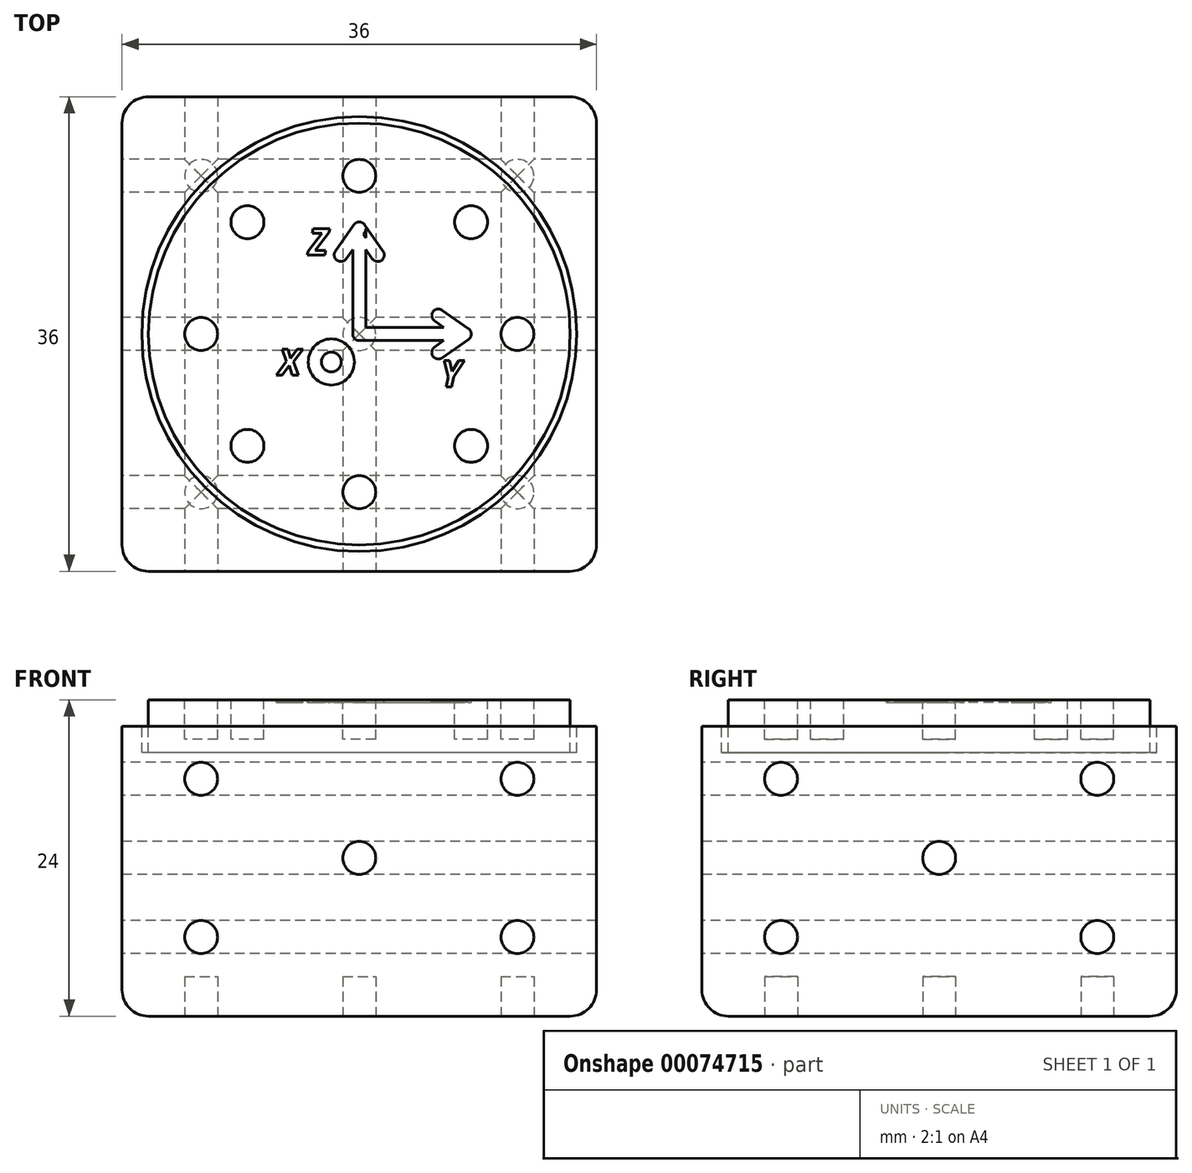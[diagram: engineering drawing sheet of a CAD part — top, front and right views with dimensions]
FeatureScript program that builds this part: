
annotation { "Feature Type Name" : "Feature", "Feature Type Description" : "" }
export const myFeature = defineFeature(function(context is Context, id is Id, definition is map)
    precondition{}
    {
        {
            var Q0;
            Q0=qCreatedBy(makeId("Right.planeOp"),FACE);
            var sketch = newSketch(context, id + "F0", { "sketchPlane" : qUnion([Q0])});
            skLineSegment(sketch, "E0.rect.bottom", {"start": v(18, -12) * mm, "end": v(-18, -12) * mm});
            skLineSegment(sketch, "E0.rect.top", {"start": v(18, 12) * mm, "end": v(-18, 12) * mm});
            skLineSegment(sketch, "E0.rect.left", {"start": v(18, -12) * mm, "end": v(18, 12) * mm});
            skLineSegment(sketch, "E0.rect.right", {"start": v(-18, -12) * mm, "end": v(-18, 12) * mm});
            skPoint(sketch, "E0.rect.middle", {"position": v(0, 0) * mm});
            skSolve(sketch);
        }
        {
            var Q0;
            Q0=makeQuery(id+"F0.imprint","IMPRINT",FACE,{"disambiguationData":[TD([[makeQuery(id+"F0.imprint","IMPRINT",EDGE,{"derivedFrom":sQuery(id+"F0.wireOp",EDGE,"E0.rect.bottom")}),-1.0]])]});
            extrude(context, id + "F1", {"entities" : qUnion([Q0]), "endBound" : BoundingType.SYMMETRIC, "depth" : 36 * mm});
        }
        {
            var Q0;
            Q0=makeQuery(id+"F1.opExtrude","SWEPT_FACE",FACE,{"disambiguationData":[OSD([sQuery(id+"F0.wireOp",EDGE,"E0.rect.right")])]});
            var sketch = newSketch(context, id + "F2", { "sketchPlane" : qUnion([Q0])});
            skLineSegment(sketch, "E1.0", {"start": v(-12, 6) * mm, "end": v(-12, -6) * mm, "construction": true});
            skLineSegment(sketch, "E1.1", {"start": v(12, 6) * mm, "end": v(-12, 6) * mm, "construction": true});
            skLineSegment(sketch, "E1.2", {"start": v(12, -6) * mm, "end": v(12, 6) * mm, "construction": true});
            skLineSegment(sketch, "E1.3", {"start": v(-12, -6) * mm, "end": v(12, -6) * mm, "construction": true});
            skLineSegment(sketch, "E2", {"start": v(-12, 6) * mm, "end": v(12, -6) * mm, "construction": true});
            skCircle(sketch, "E3", {"center": v(-12, 6) * mm, "radius": 1.25 * mm});
            skCircle(sketch, "E4", {"center": v(12, 6) * mm, "radius": 1.25 * mm});
            skCircle(sketch, "E5", {"center": v(0, 0) * mm, "radius": 1.25 * mm});
            skCircle(sketch, "E6", {"center": v(-12, -6) * mm, "radius": 1.25 * mm});
            skCircle(sketch, "E7", {"center": v(12, -6) * mm, "radius": 1.25 * mm});
            skSolve(sketch);
        }
        {
            var Q0;
            Q0=makeQuery(id+"F1.opExtrude","CAP_FACE",FACE,{"disambiguationData":[OSD([sQuery(id+"F0.wireOp",EDGE,"E0.rect.bottom"),sQuery(id+"F0.wireOp",EDGE,"E0.rect.top"),sQuery(id+"F0.wireOp",EDGE,"E0.rect.left"),sQuery(id+"F0.wireOp",EDGE,"E0.rect.right")])],"isStart":true});
            var sketch = newSketch(context, id + "F3", { "sketchPlane" : qUnion([Q0])});
            skLineSegment(sketch, "E8.0", {"start": v(-12, -6) * mm, "end": v(12, -6) * mm, "construction": true});
            skLineSegment(sketch, "E8.1", {"start": v(-12, 6) * mm, "end": v(-12, -6) * mm, "construction": true});
            skLineSegment(sketch, "E8.2", {"start": v(12, 6) * mm, "end": v(-12, 6) * mm, "construction": true});
            skLineSegment(sketch, "E8.3", {"start": v(12, -6) * mm, "end": v(12, 6) * mm, "construction": true});
            skLineSegment(sketch, "E9", {"start": v(-12, 6) * mm, "end": v(12, -6) * mm, "construction": true});
            skCircle(sketch, "E10", {"center": v(-12, 6) * mm, "radius": 1.25 * mm});
            skCircle(sketch, "E11", {"center": v(-12, -6) * mm, "radius": 1.25 * mm});
            skCircle(sketch, "E12", {"center": v(0, 0) * mm, "radius": 1.25 * mm});
            skCircle(sketch, "E13", {"center": v(12, -6) * mm, "radius": 1.25 * mm});
            skCircle(sketch, "E14", {"center": v(12, 6) * mm, "radius": 1.25 * mm});
            skSolve(sketch);
        }
        {
            var Q0;
            Q0=makeQuery(id+"F1.opExtrude","SWEPT_FACE",FACE,{"disambiguationData":[OSD([sQuery(id+"F0.wireOp",EDGE,"E0.rect.top")])]});
            var sketch = newSketch(context, id + "F4", { "sketchPlane" : qUnion([Q0])});
            skCircle(sketch, "E15", {"center": v(0, 0) * mm, "radius": 16 * mm, "construction": true});
            skCircle(sketch, "E16", {"center": v(0, 0) * mm, "radius": 12 * mm, "construction": true});
            skCircle(sketch, "E17", {"center": v(12, 0) * mm, "radius": 1.25 * mm});
            skCircle(sketch, "E18.1.0", {"center": v(8.49, 8.49) * mm, "radius": 1.25 * mm});
            skCircle(sketch, "E18.2.0", {"center": v(0, 12) * mm, "radius": 1.25 * mm});
            skCircle(sketch, "E18.3.0", {"center": v(-8.49, 8.49) * mm, "radius": 1.25 * mm});
            skCircle(sketch, "E18.4.0", {"center": v(-12, 0) * mm, "radius": 1.25 * mm});
            skCircle(sketch, "E18.5.0", {"center": v(-8.49, -8.49) * mm, "radius": 1.25 * mm});
            skCircle(sketch, "E18.6.0", {"center": v(0, -12) * mm, "radius": 1.25 * mm});
            skCircle(sketch, "E18.7.0", {"center": v(8.49, -8.49) * mm, "radius": 1.25 * mm});
            skSolve(sketch);
        }
        {
            var Q0;
            Q0=makeQuery(id+"F1.opExtrude","SWEPT_FACE",FACE,{"disambiguationData":[OSD([sQuery(id+"F0.wireOp",EDGE,"E0.rect.top")])]});
            var sketch = newSketch(context, id + "F5", { "sketchPlane" : qUnion([Q0])});
            skLineSegment(sketch, "E19.0.0", {"start": v(18, 18) * mm, "end": v(-18, 18) * mm});
            skLineSegment(sketch, "E19.0.1", {"start": v(-18, 18) * mm, "end": v(-18, -18) * mm});
            skLineSegment(sketch, "E19.0.2", {"start": v(-18, -18) * mm, "end": v(18, -18) * mm});
            skLineSegment(sketch, "E19.0.3", {"start": v(18, -18) * mm, "end": v(18, 18) * mm});
            skCircle(sketch, "E20.0", {"center": v(0, 0) * mm, "radius": 16 * mm});
            skSolve(sketch);
        }
        {
            var Q0;
            Q0=qSketchRegion(id+"F5",true);
            extrude(context, id + "F6", {"entities" : qUnion([Q0]), "operationType" : NewBodyOperationType.REMOVE, "oppositeDirection" : true, "depth" : 2 * mm});
        }
        {
            var Q0;
            Q0=makeQuery(id+"F1.opExtrude","SWEPT_FACE",FACE,{"disambiguationData":[OSD([sQuery(id+"F0.wireOp",EDGE,"E0.rect.bottom")])]});
            var sketch = newSketch(context, id + "F7", { "sketchPlane" : qUnion([Q0])});
            skLineSegment(sketch, "E21.0", {"start": v(-12, 12) * mm, "end": v(-12, -12) * mm, "construction": true});
            skLineSegment(sketch, "E21.1", {"start": v(12, 12) * mm, "end": v(-12, 12) * mm, "construction": true});
            skLineSegment(sketch, "E21.2", {"start": v(12, -12) * mm, "end": v(12, 12) * mm, "construction": true});
            skLineSegment(sketch, "E21.3", {"start": v(-12, -12) * mm, "end": v(12, -12) * mm, "construction": true});
            skLineSegment(sketch, "E22", {"start": v(-12, -12) * mm, "end": v(12, 12) * mm, "construction": true});
            skCircle(sketch, "E23", {"center": v(-12, -12) * mm, "radius": 1.25 * mm});
            skCircle(sketch, "E24", {"center": v(-12, 12) * mm, "radius": 1.25 * mm});
            skCircle(sketch, "E25", {"center": v(0, 0) * mm, "radius": 1.25 * mm});
            skCircle(sketch, "E26", {"center": v(12, -12) * mm, "radius": 1.25 * mm});
            skCircle(sketch, "E27", {"center": v(12, 12) * mm, "radius": 1.25 * mm});
            skSolve(sketch);
        }
        {
            var Q0;
            Q0=makeQuery(id+"F6.boolean.opBoolean","COPY",FACE,{"derivedFrom":makeQuery(id+"F6.opExtrude","CAP_FACE",FACE,{"disambiguationData":[OSD([sQuery(id+"F5.wireOp",EDGE,"E19.0.0"),sQuery(id+"F5.wireOp",EDGE,"E19.0.1"),sQuery(id+"F5.wireOp",EDGE,"E19.0.2"),sQuery(id+"F5.wireOp",EDGE,"E19.0.3"),sQuery(id+"F5.wireOp",EDGE,"E20.0")])],"isStart":false})});
            var sketch = newSketch(context, id + "F8", { "sketchPlane" : qUnion([Q0])});
            skCircle(sketch, "E28.0", {"center": v(0, 0) * mm, "radius": 16 * mm});
            skCircle(sketch, "E29.0", {"center": v(0, 0) * mm, "radius": 16.5 * mm});
            skSolve(sketch);
        }
        {
            var Q0;
            Q0=qSketchRegion(id+"F8",true);
            extrude(context, id + "F9", {"entities" : qUnion([Q0]), "operationType" : NewBodyOperationType.REMOVE, "oppositeDirection" : true, "depth" : 2 * mm});
        }
        {
            var Q0;
            Q0=makeQuery(id+"F1.opExtrude","CAP_EDGE",EDGE,{"disambiguationData":[OSD([sQuery(id+"F0.wireOp",EDGE,"E0.rect.right")])],"isStart":true});
            var Q1;
            Q1=makeQuery(id+"F1.opExtrude","CAP_EDGE",EDGE,{"disambiguationData":[OSD([sQuery(id+"F0.wireOp",EDGE,"E0.rect.left")])],"isStart":true});
            var Q2;
            Q2=makeQuery(id+"F1.opExtrude","CAP_EDGE",EDGE,{"disambiguationData":[OSD([sQuery(id+"F0.wireOp",EDGE,"E0.rect.right")])],"isStart":false});
            var Q3;
            Q3=makeQuery(id+"F1.opExtrude","SWEPT_FACE",FACE,{"disambiguationData":[OSD([sQuery(id+"F0.wireOp",EDGE,"E0.rect.bottom")])]});
            var Q4;
            Q4=makeQuery(id+"F1.opExtrude","CAP_EDGE",EDGE,{"disambiguationData":[OSD([sQuery(id+"F0.wireOp",EDGE,"E0.rect.left")])],"isStart":false});
            fillet(context, id + "F10", {"entities" : qUnion([Q0, Q1, Q2, Q3, Q4]), "radius" : 2 * mm, "tangentPropagation" : true, "allowEdgeOverflow" : false});
        }
        {
            var Q0;
            Q0=makeQuery(id+"F1.opExtrude","SWEPT_FACE",FACE,{"disambiguationData":[OSD([sQuery(id+"F0.wireOp",EDGE,"E0.rect.top")])]});
            var sketch = newSketch(context, id + "F11", { "sketchPlane" : qUnion([Q0])});
            skLineSegment(sketch, "E30", {"start": v(0, 8) * mm, "end": v(0, 0) * mm});
            skLineSegment(sketch, "E31", {"start": v(0, 0) * mm, "end": v(8, 0) * mm});
            skLineSegment(sketch, "E32", {"start": v(0, 8) * mm, "end": v(-1.4, 6) * mm});
            skLineSegment(sketch, "E33", {"start": v(8, 0) * mm, "end": v(6, -1.4) * mm});
            skLineSegment(sketch, "E34.MirrorCS", {"start": v(0, 8) * mm, "end": v(1.4, 6) * mm});
            skLineSegment(sketch, "E35.MirrorCS", {"start": v(8, 0) * mm, "end": v(6, 1.4) * mm});
            skArc(sketch, "E36.0.startCap", {"start": v(-0.4, 8.29) * mm, "mid": v(0.29, 8.4) * mm, "end": v(0.4, 7.71) * mm});
            skArc(sketch, "E36.0.endCap", {"start": v(-1, 5.71) * mm, "mid": v(-1.69, 5.6) * mm, "end": v(-1.8, 6.29) * mm});
            skLineSegment(sketch, "E36.0.left", {"start": v(0.4, 7.71) * mm, "end": v(-1, 5.71) * mm});
            skLineSegment(sketch, "E36.0.right", {"start": v(-0.4, 8.29) * mm, "end": v(-1.8, 6.29) * mm});
            skArc(sketch, "E36.1.startCap", {"start": v(-0.5, 8) * mm, "mid": v(0, 8.5) * mm, "end": v(0.5, 8) * mm});
            skArc(sketch, "E36.1.endCap", {"start": v(0.5, 0) * mm, "mid": v(0, -0.5) * mm, "end": v(-0.5, 0) * mm});
            skLineSegment(sketch, "E36.1.left", {"start": v(0.5, 8) * mm, "end": v(0.5, 0) * mm});
            skLineSegment(sketch, "E36.1.right", {"start": v(-0.5, 8) * mm, "end": v(-0.5, 0) * mm});
            skArc(sketch, "E36.2.startCap", {"start": v(-0.4, 7.71) * mm, "mid": v(-0.29, 8.4) * mm, "end": v(0.4, 8.29) * mm});
            skArc(sketch, "E36.2.endCap", {"start": v(1.8, 6.29) * mm, "mid": v(1.69, 5.6) * mm, "end": v(1, 5.71) * mm});
            skLineSegment(sketch, "E36.2.left", {"start": v(0.4, 8.29) * mm, "end": v(1.8, 6.29) * mm});
            skLineSegment(sketch, "E36.2.right", {"start": v(-0.4, 7.71) * mm, "end": v(1, 5.71) * mm});
            skArc(sketch, "E36.3.startCap", {"start": v(0, -0.5) * mm, "mid": v(-0.5, 0) * mm, "end": v(0, 0.5) * mm});
            skArc(sketch, "E36.3.endCap", {"start": v(8, 0.5) * mm, "mid": v(8.5, 0) * mm, "end": v(8, -0.5) * mm});
            skLineSegment(sketch, "E36.3.left", {"start": v(0, 0.5) * mm, "end": v(8, 0.5) * mm});
            skLineSegment(sketch, "E36.3.right", {"start": v(0, -0.5) * mm, "end": v(8, -0.5) * mm});
            skArc(sketch, "E36.4.startCap", {"start": v(8.29, 0.4) * mm, "mid": v(8.4, -0.29) * mm, "end": v(7.71, -0.4) * mm});
            skArc(sketch, "E36.4.endCap", {"start": v(5.71, 1) * mm, "mid": v(5.6, 1.69) * mm, "end": v(6.29, 1.8) * mm});
            skLineSegment(sketch, "E36.4.left", {"start": v(7.71, -0.4) * mm, "end": v(5.71, 1) * mm});
            skLineSegment(sketch, "E36.4.right", {"start": v(8.29, 0.4) * mm, "end": v(6.29, 1.8) * mm});
            skArc(sketch, "E36.5.startCap", {"start": v(7.71, 0.4) * mm, "mid": v(8.4, 0.29) * mm, "end": v(8.29, -0.4) * mm});
            skArc(sketch, "E36.5.endCap", {"start": v(6.29, -1.8) * mm, "mid": v(5.6, -1.69) * mm, "end": v(5.71, -1) * mm});
            skLineSegment(sketch, "E36.5.left", {"start": v(8.29, -0.4) * mm, "end": v(6.29, -1.8) * mm});
            skLineSegment(sketch, "E36.5.right", {"start": v(7.71, 0.4) * mm, "end": v(5.71, -1) * mm});
            skText(sketch, "E37", { "text": "Y", "fontName": "OpenSans-BoldItalic.ttf"});
            skText(sketch, "E38", { "text": "Z", "fontName": "OpenSans-BoldItalic.ttf"});
            skPoint(sketch, "E39", {"position": v(8, -3) * mm});
            skCircle(sketch, "E40", {"center": v(-2.12, -2.12) * mm, "radius": 0.75 * mm});
            skCircle(sketch, "E41", {"center": v(-2.12, -2.12) * mm, "radius": 1.75 * mm});
            skCircle(sketch, "E42", {"center": v(-2.12, -2.12) * mm, "radius": 1.25 * mm});
            skLineSegment(sketch, "E43", {"start": v(-2.12, -2.12) * mm, "end": v(0, 0) * mm, "construction": true});
            skLineSegment(sketch, "E44", {"start": v(0, 0) * mm, "end": v(-1.02, 0) * mm, "construction": true});
            skText(sketch, "E45", { "text": "X", "fontName": "OpenSans-BoldItalic.ttf"});
            skPoint(sketch, "E46", {"position": v(-4.1, -2.12) * mm});
            const initialGuessF11  = {"E37": [0.00618, -0.004, 1, 0, 0.002], "E38": [-0.00386, 0.006, 1, 0, 0.002], "E45": [-0.00615, -0.00312, 1, 0, 0.002]};
            skSetInitialGuess(sketch, initialGuessF11);
            skSolve(sketch);
        }
        {
            var Q0;
            Q0=qSketchRegion(id+"F11",true);
            var Q1;
            {var subQ3=sQuery(id+"F11.wireOp",EDGE,"E36.1.left");var subQ5=sQuery(id+"F11.wireOp",EDGE,"E34.MirrorCS");var subQ6=makeQuery(id+"F11.imprint","INTERSECT",VERTEX,{"derivedFrom":[subQ5,subQ3]});Q1=makeQuery(id+"F11.imprint","IMPRINT",FACE,{"disambiguationData":[TD([[makeQuery(id+"F11.imprint","IMPRINT",EDGE,{"disambiguationData":[TD([[subQ6,1.0]])],"derivedFrom":subQ5}),-1.0]])]});}
            var Q2;
            {var subQ3=sQuery(id+"F11.wireOp",EDGE,"E32");var subQ5=sQuery(id+"F11.wireOp",EDGE,"E36.1.right");var subQ7=makeQuery(id+"F11.imprint","INTERSECT",VERTEX,{"derivedFrom":[subQ3,subQ5]});Q2=makeQuery(id+"F11.imprint","IMPRINT",FACE,{"disambiguationData":[TD([[makeQuery(id+"F11.imprint","IMPRINT",EDGE,{"disambiguationData":[TD([[subQ7,1.0]])],"derivedFrom":subQ3}),1.0]])]});}
            var Q3;
            {var subQ0=sQuery(id+"F11.wireOp",EDGE,"E36.0.left");var subQ3=sQuery(id+"F11.wireOp",EDGE,"E34.MirrorCS");var subQ4=makeQuery(id+"F11.imprint","INTERSECT",VERTEX,{"derivedFrom":[subQ3,subQ0]});Q3=makeQuery(id+"F11.imprint","IMPRINT",FACE,{"disambiguationData":[TD([[makeQuery(id+"F11.imprint","IMPRINT",EDGE,{"disambiguationData":[TD([[subQ4,1.0]])],"derivedFrom":subQ3}),-1.0]])]});}
            var Q4;
            {var subQ0=sQuery(id+"F11.wireOp",EDGE,"E36.2.right");var subQ3=sQuery(id+"F11.wireOp",EDGE,"E32");var subQ4=makeQuery(id+"F11.imprint","INTERSECT",VERTEX,{"derivedFrom":[subQ3,subQ0]});Q4=makeQuery(id+"F11.imprint","IMPRINT",FACE,{"disambiguationData":[TD([[makeQuery(id+"F11.imprint","IMPRINT",EDGE,{"disambiguationData":[TD([[subQ4,1.0]])],"derivedFrom":subQ3}),1.0]])]});}
            var Q5;
            {var subQ3=sQuery(id+"F11.wireOp",EDGE,"E35.MirrorCS");var subQ5=sQuery(id+"F11.wireOp",EDGE,"E36.3.left");var subQ7=makeQuery(id+"F11.imprint","INTERSECT",VERTEX,{"derivedFrom":[subQ3,subQ5]});Q5=makeQuery(id+"F11.imprint","IMPRINT",FACE,{"disambiguationData":[TD([[makeQuery(id+"F11.imprint","IMPRINT",EDGE,{"disambiguationData":[TD([[subQ7,1.0]])],"derivedFrom":subQ3}),1.0]])]});}
            var Q6;
            {var subQ0=sQuery(id+"F11.wireOp",EDGE,"E36.5.right");var subQ3=sQuery(id+"F11.wireOp",EDGE,"E35.MirrorCS");var subQ4=makeQuery(id+"F11.imprint","INTERSECT",VERTEX,{"derivedFrom":[subQ3,subQ0]});Q6=makeQuery(id+"F11.imprint","IMPRINT",FACE,{"disambiguationData":[TD([[makeQuery(id+"F11.imprint","IMPRINT",EDGE,{"disambiguationData":[TD([[subQ4,1.0]])],"derivedFrom":subQ3}),1.0]])]});}
            var Q7;
            {var subQ1=sQuery(id+"F11.wireOp",EDGE,"E35.MirrorCS");var subQ5=sQuery(id+"F11.wireOp",EDGE,"E36.3.left");var subQ7=makeQuery(id+"F11.imprint","INTERSECT",VERTEX,{"derivedFrom":[subQ1,subQ5]});Q7=makeQuery(id+"F11.imprint","IMPRINT",FACE,{"disambiguationData":[TD([[makeQuery(id+"F11.imprint","IMPRINT",EDGE,{"disambiguationData":[TD([[subQ7,1.0]])],"derivedFrom":subQ1}),-1.0]])]});}
            var Q8;
            {var subQ0=sQuery(id+"F11.wireOp",EDGE,"E36.4.left");var subQ3=sQuery(id+"F11.wireOp",EDGE,"E33");var subQ4=makeQuery(id+"F11.imprint","INTERSECT",VERTEX,{"derivedFrom":[subQ3,subQ0]});Q8=makeQuery(id+"F11.imprint","IMPRINT",FACE,{"disambiguationData":[TD([[makeQuery(id+"F11.imprint","IMPRINT",EDGE,{"disambiguationData":[TD([[subQ4,1.0]])],"derivedFrom":subQ3}),-1.0]])]});}
            var Q9;
            {var subQ1=sQuery(id+"F11.wireOp",EDGE,"E33");var subQ5=sQuery(id+"F11.wireOp",EDGE,"E36.3.right");var subQ7=makeQuery(id+"F11.imprint","INTERSECT",VERTEX,{"derivedFrom":[subQ1,subQ5]});Q9=makeQuery(id+"F11.imprint","IMPRINT",FACE,{"disambiguationData":[TD([[makeQuery(id+"F11.imprint","IMPRINT",EDGE,{"disambiguationData":[TD([[subQ7,1.0]])],"derivedFrom":subQ1}),1.0]])]});}
            var Q10;
            {var subQ3=sQuery(id+"F11.wireOp",EDGE,"E36.0.startCap");Q10=makeQuery(id+"F11.imprint","IMPRINT",FACE,{"disambiguationData":[TD([[makeQuery(id+"F11.imprint","IMPRINT",EDGE,{"derivedFrom":subQ3}),1.0]])]});}
            var Q11;
            {var subQ1=sQuery(id+"F11.wireOp",EDGE,"E32");var subQ5=sQuery(id+"F11.wireOp",EDGE,"E36.1.right");var subQ7=makeQuery(id+"F11.imprint","INTERSECT",VERTEX,{"derivedFrom":[subQ1,subQ5]});Q11=makeQuery(id+"F11.imprint","IMPRINT",FACE,{"disambiguationData":[TD([[makeQuery(id+"F11.imprint","IMPRINT",EDGE,{"disambiguationData":[TD([[subQ7,1.0]])],"derivedFrom":subQ1}),-1.0]])]});}
            var Q12;
            Q12=makeQuery(id+"F11.imprint","IMPRINT",FACE,{"disambiguationData":[TD([[makeQuery(id+"F11.imprint","IMPRINT",EDGE,{"derivedFrom":sQuery(id+"F11.wireOp",EDGE,"E40")}),-1.0]])]});
            extrude(context, id + "F12", {"entities" : qUnion([Q0, Q1, Q2, Q3, Q4, Q5, Q6, Q7, Q8, Q9, Q10, Q11, Q12]), "operationType" : NewBodyOperationType.REMOVE, "oppositeDirection" : true, "depth" : 0.2 * mm});
        }
        {
            var Q0;
            Q0=qSketchRegion(id+"F2",true);
            extrude(context, id + "F13", {"entities" : qUnion([Q0]), "operationType" : NewBodyOperationType.REMOVE, "endBound" : BoundingType.THROUGH_ALL, "oppositeDirection" : true, "depth" : 25 * mm});
        }
        {
            var Q0;
            Q0=qSketchRegion(id+"F3",true);
            extrude(context, id + "F14", {"entities" : qUnion([Q0]), "operationType" : NewBodyOperationType.REMOVE, "endBound" : BoundingType.THROUGH_ALL, "oppositeDirection" : true, "depth" : 25 * mm});
        }
        {
            var Q0;
            Q0=qSketchRegion(id+"F4",true);
            extrude(context, id + "F15", {"entities" : qUnion([Q0]), "operationType" : NewBodyOperationType.REMOVE, "oppositeDirection" : true, "depth" : 3 * mm});
        }
        {
            var Q0;
            Q0=qSketchRegion(id+"F7",true);
            extrude(context, id + "F16", {"entities" : qUnion([Q0]), "operationType" : NewBodyOperationType.REMOVE, "oppositeDirection" : true, "depth" : 3 * mm});
        }
    });
